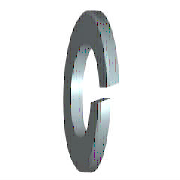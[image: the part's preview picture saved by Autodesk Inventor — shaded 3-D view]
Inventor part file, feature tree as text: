
AUTODESK INVENTOR PART (.ipt)
format: ipt  version: 2021 (Build 250183000, 183)  size: 126,464 bytes
history: native  units: mm (DEFAULTED — no unit token found)
features: sketch x2, extrude x1, other x1, plane x1
ambient origin geometry x6: Origin, YZ Plane, X Axis, Y Axis, Z Axis, Center Point
bodies: Solid1 (feature_tree), Body (feature_tree)
feature tree (5):
  extrude  "Cut"  Depth=27.4mm
  other  "Work Axis1"
  plane  "Work Plane1"
  sketch  "Sketch1"  dims[d0=16.2mm d1=27.4mm]
  sketch  "Sketch2"  dims[d2=3.7mm d3=0.0mm d4=0.74mm d5=0.74mm d6=12.217305mm d7=3.7mm d8=0.0mm d9=0.0mm d10=0.0mm d11=0.0mm d12=0.0mm]
